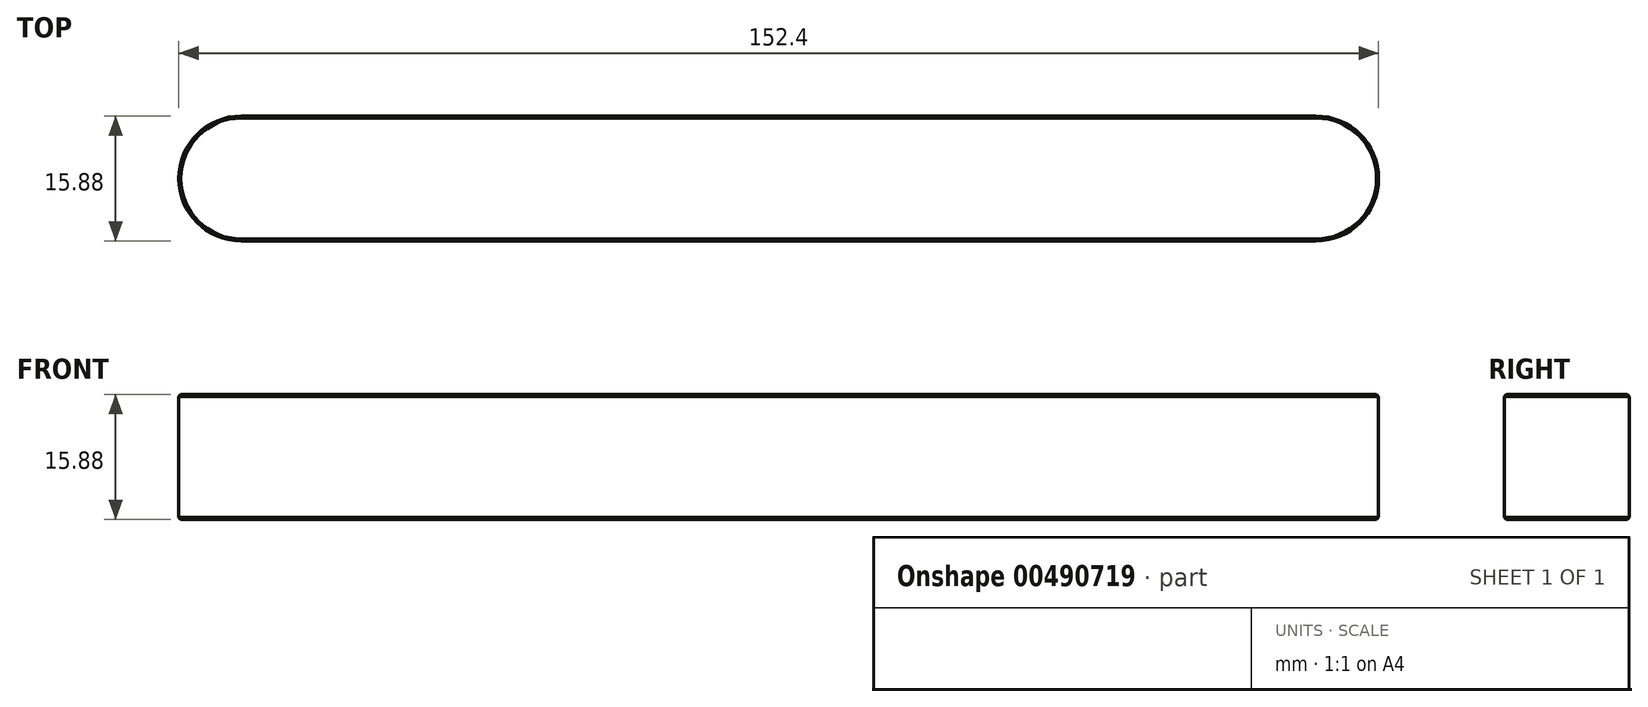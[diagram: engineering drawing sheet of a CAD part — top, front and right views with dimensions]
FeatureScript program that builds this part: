
annotation { "Feature Type Name" : "Feature", "Feature Type Description" : "" }
export const myFeature = defineFeature(function(context is Context, id is Id, definition is map)
    precondition{}
    {
        {
            var Q0;
            Q0=qCreatedBy(makeId("Top.planeOp"),FACE);
            var sketch = newSketch(context, id + "F0", { "sketchPlane" : qUnion([Q0])});
            skLineSegment(sketch, "E0.bottom", {"start": v(76.2, -7.94) * mm, "end": v(-76.2, -7.94) * mm});
            skLineSegment(sketch, "E0.top", {"start": v(76.2, 7.94) * mm, "end": v(-76.2, 7.94) * mm});
            skLineSegment(sketch, "E0.left", {"start": v(76.2, -7.94) * mm, "end": v(76.2, 7.94) * mm});
            skLineSegment(sketch, "E0.right", {"start": v(-76.2, -7.94) * mm, "end": v(-76.2, 7.94) * mm});
            skPoint(sketch, "E0.middle", {"position": v(0, 0) * mm});
            skSolve(sketch);
        }
        {
            var Q0;
            Q0 = qSketchRegion(id + "F0", true);
            extrude(context, id + "F1", {"entities" : qUnion([Q0]), "depth" : 15.88 * mm});
        }
        {
            var Q0;
            Q0=makeQuery(id+"F1.opExtrude","SWEPT_EDGE",EDGE,{"disambiguationData":[OSD([sQuery(id+"F0.wireOp",EDGE,"E0.top"),sQuery(id+"F0.wireOp",EDGE,"E0.right")])]});
            var Q1;
            Q1=makeQuery(id+"F1.opExtrude","SWEPT_EDGE",EDGE,{"disambiguationData":[OSD([sQuery(id+"F0.wireOp",EDGE,"E0.bottom"),sQuery(id+"F0.wireOp",EDGE,"E0.right")])]});
            var Q2;
            Q2=makeQuery(id+"F1.opExtrude","SWEPT_EDGE",EDGE,{"disambiguationData":[OSD([sQuery(id+"F0.wireOp",EDGE,"E0.bottom"),sQuery(id+"F0.wireOp",EDGE,"E0.left")])]});
            var Q3;
            Q3=makeQuery(id+"F1.opExtrude","SWEPT_EDGE",EDGE,{"disambiguationData":[OSD([sQuery(id+"F0.wireOp",EDGE,"E0.top"),sQuery(id+"F0.wireOp",EDGE,"E0.left")])]});
            fillet(context, id + "F2", {"entities" : qUnion([Q0, Q1, Q2, Q3]), "radius" : 7.94 * mm, "tangentPropagation" : true, "allowEdgeOverflow" : false});
        }
        {
            var Q0;
            Q0=makeQuery(id+"F1.opExtrude","CAP_FACE",FACE,{"disambiguationData":[OSD([sQuery(id+"F0.wireOp",EDGE,"E0.bottom"),sQuery(id+"F0.wireOp",EDGE,"E0.top"),sQuery(id+"F0.wireOp",EDGE,"E0.left"),sQuery(id+"F0.wireOp",EDGE,"E0.right")])],"isStart":true});
            var Q1;
            Q1=makeQuery(id+"F1.opExtrude","CAP_FACE",FACE,{"disambiguationData":[OSD([sQuery(id+"F0.wireOp",EDGE,"E0.bottom"),sQuery(id+"F0.wireOp",EDGE,"E0.top"),sQuery(id+"F0.wireOp",EDGE,"E0.left"),sQuery(id+"F0.wireOp",EDGE,"E0.right")])],"isStart":false});
            chamfer(context, id + "F3", {"entities" : qUnion([Q0, Q1]), "width" : 0.25 * mm, "tangentPropagation" : true});
        }
    });
